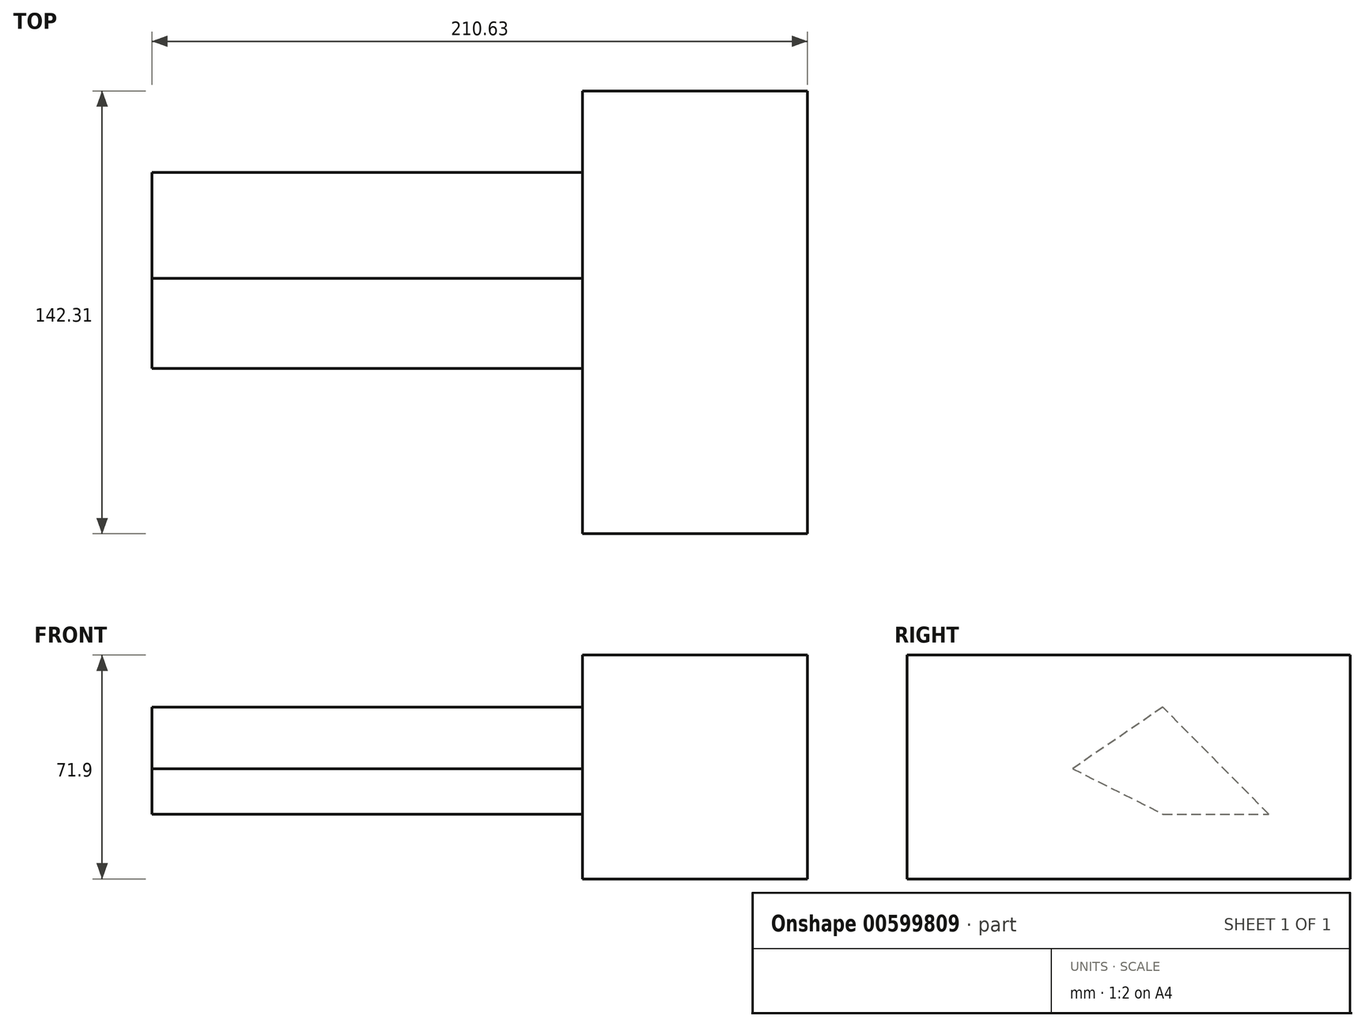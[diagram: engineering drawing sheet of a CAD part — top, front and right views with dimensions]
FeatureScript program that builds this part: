
annotation { "Feature Type Name" : "Feature", "Feature Type Description" : "" }
export const myFeature = defineFeature(function(context is Context, id is Id, definition is map)
    precondition{}
    {
        {
            var Q0;
            Q0=qCreatedBy(makeId("Top.planeOp"),FACE);
            var sketch = newSketch(context, id + "F0", { "sketchPlane" : qUnion([Q0])});
            skLineSegment(sketch, "E0.bottom", {"start": v(-49.63, 0) * mm, "end": v(22.66, 0) * mm});
            skLineSegment(sketch, "E0.top", {"start": v(-49.63, 142.31) * mm, "end": v(22.66, 142.31) * mm});
            skLineSegment(sketch, "E0.left", {"start": v(-49.63, 0) * mm, "end": v(-49.63, 142.31) * mm});
            skLineSegment(sketch, "E0.right", {"start": v(22.66, 0) * mm, "end": v(22.66, 142.31) * mm});
            skSolve(sketch);
        }
        {
            var Q0;
            Q0 = qSketchRegion(id + "F0", true);
            extrude(context, id + "F1", {"entities" : qUnion([Q0]), "depth" : 71.9 * mm, "offsetDistance" : 25 * mm});
        }
        {
            var Q0;
            Q0=makeQuery(id+"F1.opExtrude","SWEPT_FACE",FACE,{"disambiguationData":[OSD([sQuery(id+"F0.wireOp",EDGE,"E0.left")])]});
            var sketch = newSketch(context, id + "F2", { "sketchPlane" : qUnion([Q0])});
            skLineSegment(sketch, "E1", {"start": v(-82.11, 20.83) * mm, "end": v(-116.11, 20.83) * mm});
            skLineSegment(sketch, "E2", {"start": v(-116.11, 20.83) * mm, "end": v(-82.11, 55.19) * mm});
            skLineSegment(sketch, "E3", {"start": v(-53.13, 35.42) * mm, "end": v(-82.11, 20.83) * mm});
            skLineSegment(sketch, "E4", {"start": v(-82.11, 55.19) * mm, "end": v(-53.13, 35.42) * mm});
            skSolve(sketch);
        }
        {
            var Q0;
            Q0=makeQuery(id+"F2.imprint","IMPRINT",FACE,{"disambiguationData":[TD([[makeQuery(id+"F2.imprint","IMPRINT",EDGE,{"derivedFrom":sQuery(id+"F2.wireOp",EDGE,"E1")}),-1.0]])]});
            extrude(context, id + "F3", {"entities" : qUnion([Q0]), "operationType" : NewBodyOperationType.ADD, "depth" : 138.34 * mm, "offsetDistance" : 25 * mm});
        }
    });
